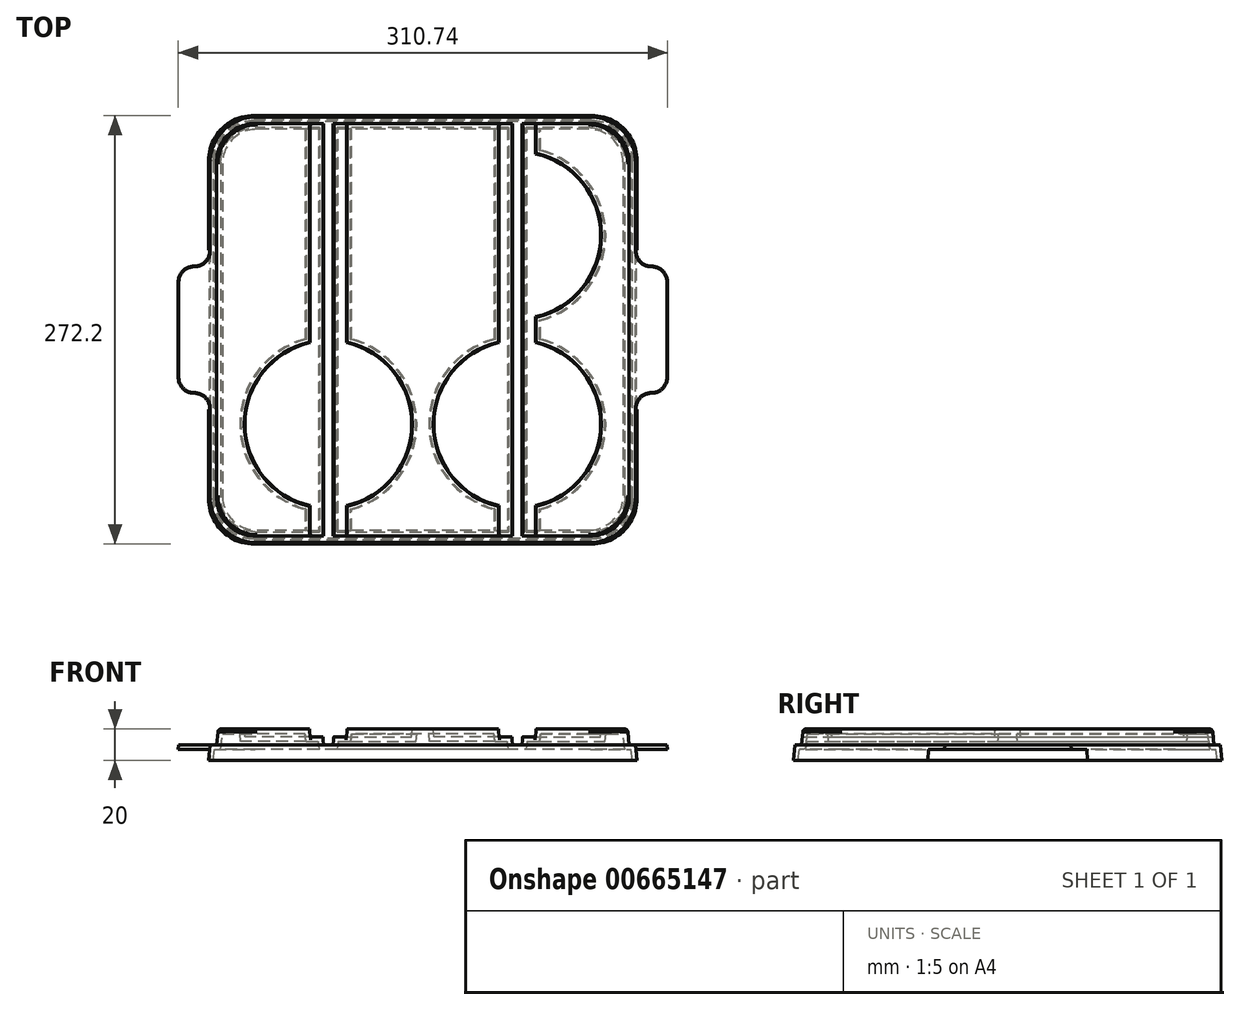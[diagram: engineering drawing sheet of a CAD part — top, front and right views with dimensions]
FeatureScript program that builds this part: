
annotation { "Feature Type Name" : "Feature", "Feature Type Description" : "" }
export const myFeature = defineFeature(function(context is Context, id is Id, definition is map)
    precondition{}
    {
        {
            var Q0;
            Q0=qCreatedBy(makeId("Top.planeOp"),FACE);
            var sketch = newSketch(context, id + "F0", { "sketchPlane" : qUnion([Q0])});
            skLineSegment(sketch, "E0", {"start": v(-60, 63.68) * mm, "end": v(-60, -68.5) * mm, "construction": true});
            skLineSegment(sketch, "E1", {"start": v(-108.87, 60) * mm, "end": v(91.95, 60) * mm, "construction": true});
            skLineSegment(sketch, "E2.MirrorCS", {"start": v(60, 63.68) * mm, "end": v(60, -68.5) * mm, "construction": true});
            skLineSegment(sketch, "E3.MirrorCS", {"start": v(-108.87, -60) * mm, "end": v(91.95, -60) * mm, "construction": true});
            skLineSegment(sketch, "E4", {"start": v(-130, 152.73) * mm, "end": v(-130, -156.18) * mm, "construction": true});
            skLineSegment(sketch, "E5", {"start": v(-201.2, -130) * mm, "end": v(310.8, -130) * mm, "construction": true});
            skLineSegment(sketch, "E6.MirrorCS", {"start": v(130, 152.73) * mm, "end": v(130, -156.18) * mm, "construction": true});
            skLineSegment(sketch, "E7.MirrorCS", {"start": v(-201.2, 130) * mm, "end": v(310.8, 130) * mm, "construction": true});
            skLineSegment(sketch, "E8.bottom", {"start": v(-130, 130) * mm, "end": v(130, 130) * mm});
            skLineSegment(sketch, "E8.top", {"start": v(-130, -130) * mm, "end": v(130, -130) * mm});
            skLineSegment(sketch, "E8.left", {"start": v(-130, 130) * mm, "end": v(-130, -130) * mm});
            skLineSegment(sketch, "E8.right", {"start": v(130, 130) * mm, "end": v(130, -130) * mm});
            skSolve(sketch);
        }
        {
            var Q0;
            Q0=makeQuery(id+"F0.imprint","IMPRINT",FACE,{"disambiguationData":[TD([[makeQuery(id+"F0.imprint","IMPRINT",EDGE,{"derivedFrom":sQuery(id+"F0.wireOp",EDGE,"E8.bottom")}),-1.0]])]});
            extrude(context, id + "F1", {"entities" : qUnion([Q0]), "oppositeDirection" : true, "depth" : 10 * mm, "offsetDistance" : 25 * mm, "hasDraft" : true, "draftAngle" : 6 * degree});
        }
        {
            var Q0;
            Q0=makeQuery(id+"F1.opExtrude","CAP_FACE",FACE,{"disambiguationData":[OSD([sQuery(id+"F0.wireOp",EDGE,"E8.bottom"),sQuery(id+"F0.wireOp",EDGE,"E8.top"),sQuery(id+"F0.wireOp",EDGE,"E8.left"),sQuery(id+"F0.wireOp",EDGE,"E8.right")])],"isStart":false});
            var sketch = newSketch(context, id + "F2", { "sketchPlane" : qUnion([Q0])});
            skLineSegment(sketch, "E9", {"start": v(-264, 135.05) * mm, "end": v(236, 135.05) * mm, "construction": true});
            skLineSegment(sketch, "E10.MirrorCS", {"start": v(-264, -135.05) * mm, "end": v(236, -135.05) * mm, "construction": true});
            skLineSegment(sketch, "E11", {"start": v(-135.05, 316.9) * mm, "end": v(-135.05, -183.1) * mm, "construction": true});
            skLineSegment(sketch, "E12.MirrorCS", {"start": v(135.05, 316.9) * mm, "end": v(135.05, -183.1) * mm, "construction": true});
            skLineSegment(sketch, "E13.bottom", {"start": v(-135.05, 135.05) * mm, "end": v(135.05, 135.05) * mm});
            skLineSegment(sketch, "E13.top", {"start": v(-135.05, -135.05) * mm, "end": v(135.05, -135.05) * mm});
            skLineSegment(sketch, "E13.left", {"start": v(-135.05, 135.05) * mm, "end": v(-135.05, -135.05) * mm});
            skLineSegment(sketch, "E13.right", {"start": v(135.05, 135.05) * mm, "end": v(135.05, -135.05) * mm});
            skSolve(sketch);
        }
        {
            var Q0;
            Q0=makeQuery(id+"F2.imprint","IMPRINT",FACE,{"disambiguationData":[TD([[makeQuery(id+"F2.imprint","IMPRINT",EDGE,{"derivedFrom":sQuery(id+"F2.wireOp",EDGE,"E13.bottom")}),-1.0]])]});
            var Q1;
            Q1=makeQuery(id+"F2.imprint","IMPRINT",FACE,{"disambiguationData":[TD([[makeQuery(id+"F2.imprint","IMPRINT",EDGE,{"derivedFrom":makeQuery(id+"F1.opExtrude","CAP_EDGE",EDGE,{"disambiguationData":[OSD([sQuery(id+"F0.wireOp",EDGE,"E8.bottom")])],"isStart":false})}),1.0]])]});
            extrude(context, id + "F3", {"entities" : qUnion([Q0, Q1]), "operationType" : NewBodyOperationType.ADD, "depth" : 10 * mm, "offsetDistance" : 25 * mm, "hasDraft" : true, "draftAngle" : 6 * degree});
        }
        {
            var Q0;
            Q0=makeQuery(id+"F1.opExtrude","CAP_FACE",FACE,{"disambiguationData":[OSD([sQuery(id+"F0.wireOp",EDGE,"E8.bottom"),sQuery(id+"F0.wireOp",EDGE,"E8.top"),sQuery(id+"F0.wireOp",EDGE,"E8.left"),sQuery(id+"F0.wireOp",EDGE,"E8.right")])],"isStart":true});
            var sketch = newSketch(context, id + "F4", { "sketchPlane" : qUnion([Q0])});
            skLineSegment(sketch, "E14", {"start": v(-130, 0) * mm, "end": v(130, 0) * mm, "construction": true});
            skLineSegment(sketch, "E15", {"start": v(-130, -60) * mm, "end": v(130, -60) * mm, "construction": true});
            skLineSegment(sketch, "E16.MirrorCS", {"start": v(-130, 60) * mm, "end": v(130, 60) * mm, "construction": true});
            skLineSegment(sketch, "E17", {"start": v(-60, -130) * mm, "end": v(-60, 130) * mm, "construction": true});
            skLineSegment(sketch, "E18", {"start": v(0, -130) * mm, "end": v(0, 130) * mm, "construction": true});
            skLineSegment(sketch, "E19.MirrorCS", {"start": v(60, -130) * mm, "end": v(60, 130) * mm, "construction": true});
            skCircle(sketch, "E20", {"center": v(-60, -60) * mm, "radius": 53.5 * mm});
            skCircle(sketch, "E21", {"center": v(-60, 60) * mm, "radius": 53.5 * mm});
            skCircle(sketch, "E22", {"center": v(60, 60) * mm, "radius": 53.5 * mm});
            skCircle(sketch, "E23", {"center": v(60, -60) * mm, "radius": 53.5 * mm});
            skLineSegment(sketch, "E24", {"start": v(72, 150) * mm, "end": v(72, 105.96) * mm});
            skLineSegment(sketch, "E25.MirrorCS", {"start": v(48, 130) * mm, "end": v(48, 105.96) * mm});
            skLineSegment(sketch, "E26.MirrorCS", {"start": v(-48, 130) * mm, "end": v(-48, 105.96) * mm});
            skLineSegment(sketch, "E27.MirrorCS", {"start": v(-72, 130) * mm, "end": v(-72, 105.96) * mm});
            skLineSegment(sketch, "E28.MirrorCS", {"start": v(48, -130) * mm, "end": v(48, -105.96) * mm});
            skLineSegment(sketch, "E29.MirrorCS", {"start": v(72, -130) * mm, "end": v(72, -105.96) * mm});
            skLineSegment(sketch, "E30.MirrorCS", {"start": v(-72, -130) * mm, "end": v(-72, -105.96) * mm});
            skLineSegment(sketch, "E31.MirrorCS", {"start": v(-48, -130) * mm, "end": v(-48, -105.96) * mm});
            skPoint(sketch, "E32.orphan", {"position": v(72, 130) * mm});
            skLineSegment(sketch, "E33.MirrorCS", {"start": v(48, 150) * mm, "end": v(48, 105.96) * mm});
            skLineSegment(sketch, "E34.MirrorCS", {"start": v(-48, 150) * mm, "end": v(-48, 105.96) * mm});
            skLineSegment(sketch, "E35.MirrorCS", {"start": v(-72, 150) * mm, "end": v(-72, 105.96) * mm});
            skLineSegment(sketch, "E36.MirrorCS", {"start": v(-48, -150) * mm, "end": v(-48, -105.96) * mm});
            skLineSegment(sketch, "E37.MirrorCS", {"start": v(-72, -150) * mm, "end": v(-72, -105.96) * mm});
            skLineSegment(sketch, "E38.MirrorCS", {"start": v(48, -150) * mm, "end": v(48, -105.96) * mm});
            skLineSegment(sketch, "E39.MirrorCS", {"start": v(72, -150) * mm, "end": v(72, -105.96) * mm});
            skLineSegment(sketch, "E40", {"start": v(-72, 150) * mm, "end": v(-48, 150) * mm});
            skLineSegment(sketch, "E41", {"start": v(48, 150) * mm, "end": v(72, 150) * mm});
            skLineSegment(sketch, "E42", {"start": v(-72, -150) * mm, "end": v(-48, -150) * mm});
            skLineSegment(sketch, "E43", {"start": v(48, -150) * mm, "end": v(72, -150) * mm});
            skLineSegment(sketch, "E44", {"start": v(-72, 105.96) * mm, "end": v(-72, -105.96) * mm});
            skLineSegment(sketch, "E45.MirrorCS", {"start": v(-48, 105.96) * mm, "end": v(-48, -105.96) * mm});
            skLineSegment(sketch, "E46.MirrorCS", {"start": v(48, 105.96) * mm, "end": v(48, -105.96) * mm});
            skLineSegment(sketch, "E47.MirrorCS", {"start": v(72, 105.96) * mm, "end": v(72, -105.96) * mm});
            skLineSegment(sketch, "E48", {"start": v(-64, 150) * mm, "end": v(-64, -150) * mm});
            skPoint(sketch, "E48.endSnap0", {"position": v(-60, -150) * mm});
            skLineSegment(sketch, "E49.MirrorCS", {"start": v(-56, 150) * mm, "end": v(-56, -150) * mm});
            skLineSegment(sketch, "E50.MirrorCS", {"start": v(56, 150) * mm, "end": v(56, -150) * mm});
            skLineSegment(sketch, "E51.MirrorCS", {"start": v(64, 150) * mm, "end": v(64, -150) * mm});
            skSolve(sketch);
        }
        {
            var Q0;
            {var subQ0=sQuery(id+"F4.wireOp",EDGE,"E34.MirrorCS");var subQ1=sQuery(id+"F4.wireOp",EDGE,"E21");var subQ2=makeQuery(id+"F4.imprint","INTERSECT",VERTEX,{"derivedFrom":[subQ1,subQ0]});Q0=makeQuery(id+"F4.imprint","IMPRINT",FACE,{"disambiguationData":[TD([[makeQuery(id+"F4.imprint","IMPRINT",EDGE,{"disambiguationData":[TD([[subQ2,1.0]])],"derivedFrom":subQ1}),1.0]])]});}
            var Q1;
            {var subQ0=sQuery(id+"F4.wireOp",EDGE,"E35.MirrorCS");var subQ1=sQuery(id+"F4.wireOp",EDGE,"E21");var subQ2=makeQuery(id+"F4.imprint","INTERSECT",VERTEX,{"derivedFrom":[subQ1,subQ0]});Q1=makeQuery(id+"F4.imprint","IMPRINT",FACE,{"disambiguationData":[TD([[makeQuery(id+"F4.imprint","IMPRINT",EDGE,{"disambiguationData":[TD([[subQ2,-1.0]])],"derivedFrom":subQ1}),1.0]])]});}
            var Q2;
            {var subQ3=sQuery(id+"F4.wireOp",EDGE,"E21");var subQ6=sQuery(id+"F4.wireOp",EDGE,"E48");var subQ7=makeQuery(id+"F4.imprint","INTERSECT",VERTEX,{"disambiguationData":[OD(0.0)],"derivedFrom":[subQ3,subQ6]});Q2=makeQuery(id+"F4.imprint","IMPRINT",FACE,{"disambiguationData":[TD([[makeQuery(id+"F4.imprint","IMPRINT",EDGE,{"disambiguationData":[TD([[subQ7,-1.0]])],"derivedFrom":subQ3}),1.0]])]});}
            var Q3;
            {var subQ3=sQuery(id+"F4.wireOp",EDGE,"E21");var subQ6=sQuery(id+"F4.wireOp",EDGE,"E49.MirrorCS");var subQ8=makeQuery(id+"F4.imprint","INTERSECT",VERTEX,{"disambiguationData":[OD(0.0)],"derivedFrom":[subQ3,subQ6]});Q3=makeQuery(id+"F4.imprint","IMPRINT",FACE,{"disambiguationData":[TD([[makeQuery(id+"F4.imprint","IMPRINT",EDGE,{"disambiguationData":[TD([[subQ8,1.0]])],"derivedFrom":subQ3}),1.0]])]});}
            var Q4;
            {var subQ0=sQuery(id+"F4.wireOp",EDGE,"E49.MirrorCS");var subQ1=sQuery(id+"F4.wireOp",EDGE,"E21");var subQ2=makeQuery(id+"F4.imprint","INTERSECT",VERTEX,{"disambiguationData":[OD(0.0)],"derivedFrom":[subQ1,subQ0]});Q4=makeQuery(id+"F4.imprint","IMPRINT",FACE,{"disambiguationData":[TD([[makeQuery(id+"F4.imprint","IMPRINT",EDGE,{"disambiguationData":[TD([[subQ2,-1.0]])],"derivedFrom":subQ1}),1.0]])]});}
            var Q5;
            {var subQ0=sQuery(id+"F4.wireOp",EDGE,"E33.MirrorCS");var subQ1=sQuery(id+"F4.wireOp",EDGE,"E22");var subQ2=makeQuery(id+"F4.imprint","INTERSECT",VERTEX,{"derivedFrom":[subQ1,subQ0]});Q5=makeQuery(id+"F4.imprint","IMPRINT",FACE,{"disambiguationData":[TD([[makeQuery(id+"F4.imprint","IMPRINT",EDGE,{"disambiguationData":[TD([[subQ2,-1.0]])],"derivedFrom":subQ1}),1.0]])]});}
            var Q6;
            {var subQ3=sQuery(id+"F4.wireOp",EDGE,"E22");var subQ5=sQuery(id+"F4.wireOp",EDGE,"E50.MirrorCS");var subQ6=makeQuery(id+"F4.imprint","INTERSECT",VERTEX,{"disambiguationData":[OD(0.0)],"derivedFrom":[subQ3,subQ5]});Q6=makeQuery(id+"F4.imprint","IMPRINT",FACE,{"disambiguationData":[TD([[makeQuery(id+"F4.imprint","IMPRINT",EDGE,{"disambiguationData":[TD([[subQ6,-1.0]])],"derivedFrom":subQ3}),1.0]])]});}
            var Q7;
            {var subQ3=sQuery(id+"F4.wireOp",EDGE,"E22");var subQ6=sQuery(id+"F4.wireOp",EDGE,"E51.MirrorCS");var subQ8=makeQuery(id+"F4.imprint","INTERSECT",VERTEX,{"disambiguationData":[OD(0.0)],"derivedFrom":[subQ3,subQ6]});Q7=makeQuery(id+"F4.imprint","IMPRINT",FACE,{"disambiguationData":[TD([[makeQuery(id+"F4.imprint","IMPRINT",EDGE,{"disambiguationData":[TD([[subQ8,1.0]])],"derivedFrom":subQ3}),1.0]])]});}
            var Q8;
            {var subQ0=sQuery(id+"F4.wireOp",EDGE,"E51.MirrorCS");var subQ1=sQuery(id+"F4.wireOp",EDGE,"E22");var subQ2=makeQuery(id+"F4.imprint","INTERSECT",VERTEX,{"disambiguationData":[OD(0.0)],"derivedFrom":[subQ1,subQ0]});Q8=makeQuery(id+"F4.imprint","IMPRINT",FACE,{"disambiguationData":[TD([[makeQuery(id+"F4.imprint","IMPRINT",EDGE,{"disambiguationData":[TD([[subQ2,-1.0]])],"derivedFrom":subQ1}),1.0]])]});}
            var Q9;
            {var subQ0=sQuery(id+"F4.wireOp",EDGE,"E24");var subQ1=sQuery(id+"F4.wireOp",EDGE,"E22");var subQ2=makeQuery(id+"F4.imprint","INTERSECT",VERTEX,{"derivedFrom":[subQ1,subQ0]});Q9=makeQuery(id+"F4.imprint","IMPRINT",FACE,{"disambiguationData":[TD([[makeQuery(id+"F4.imprint","IMPRINT",EDGE,{"disambiguationData":[TD([[subQ2,1.0]])],"derivedFrom":subQ1}),1.0]])]});}
            var Q10;
            {var subQ0=sQuery(id+"F4.wireOp",EDGE,"E44");var subQ1=sQuery(id+"F4.wireOp",EDGE,"E20");var subQ2=makeQuery(id+"F4.imprint","INTERSECT",VERTEX,{"derivedFrom":[subQ1,subQ0]});Q10=makeQuery(id+"F4.imprint","IMPRINT",FACE,{"disambiguationData":[TD([[makeQuery(id+"F4.imprint","IMPRINT",EDGE,{"disambiguationData":[TD([[subQ2,-1.0]])],"derivedFrom":subQ1}),1.0]])]});}
            var Q11;
            {var subQ3=sQuery(id+"F4.wireOp",EDGE,"E20");var subQ6=sQuery(id+"F4.wireOp",EDGE,"E48");var subQ8=makeQuery(id+"F4.imprint","INTERSECT",VERTEX,{"disambiguationData":[OD(0.0)],"derivedFrom":[subQ3,subQ6]});Q11=makeQuery(id+"F4.imprint","IMPRINT",FACE,{"disambiguationData":[TD([[makeQuery(id+"F4.imprint","IMPRINT",EDGE,{"disambiguationData":[TD([[subQ8,-1.0]])],"derivedFrom":subQ3}),1.0]])]});}
            var Q12;
            {var subQ0=sQuery(id+"F4.wireOp",EDGE,"E49.MirrorCS");var subQ1=sQuery(id+"F4.wireOp",EDGE,"E20");var subQ2=makeQuery(id+"F4.imprint","INTERSECT",VERTEX,{"disambiguationData":[OD(0.0)],"derivedFrom":[subQ1,subQ0]});Q12=makeQuery(id+"F4.imprint","IMPRINT",FACE,{"disambiguationData":[TD([[makeQuery(id+"F4.imprint","IMPRINT",EDGE,{"disambiguationData":[TD([[subQ2,-1.0]])],"derivedFrom":subQ1}),1.0]])]});}
            var Q13;
            {var subQ3=sQuery(id+"F4.wireOp",EDGE,"E20");var subQ6=sQuery(id+"F4.wireOp",EDGE,"E49.MirrorCS");var subQ8=makeQuery(id+"F4.imprint","INTERSECT",VERTEX,{"disambiguationData":[OD(0.0)],"derivedFrom":[subQ3,subQ6]});Q13=makeQuery(id+"F4.imprint","IMPRINT",FACE,{"disambiguationData":[TD([[makeQuery(id+"F4.imprint","IMPRINT",EDGE,{"disambiguationData":[TD([[subQ8,1.0]])],"derivedFrom":subQ3}),1.0]])]});}
            var Q14;
            {var subQ0=sQuery(id+"F4.wireOp",EDGE,"E45.MirrorCS");var subQ1=sQuery(id+"F4.wireOp",EDGE,"E20");var subQ2=makeQuery(id+"F4.imprint","INTERSECT",VERTEX,{"derivedFrom":[subQ1,subQ0]});Q14=makeQuery(id+"F4.imprint","IMPRINT",FACE,{"disambiguationData":[TD([[makeQuery(id+"F4.imprint","IMPRINT",EDGE,{"disambiguationData":[TD([[subQ2,1.0]])],"derivedFrom":subQ1}),1.0]])]});}
            var Q15;
            {var subQ0=sQuery(id+"F4.wireOp",EDGE,"E46.MirrorCS");var subQ1=sQuery(id+"F4.wireOp",EDGE,"E23");var subQ2=makeQuery(id+"F4.imprint","INTERSECT",VERTEX,{"derivedFrom":[subQ1,subQ0]});Q15=makeQuery(id+"F4.imprint","IMPRINT",FACE,{"disambiguationData":[TD([[makeQuery(id+"F4.imprint","IMPRINT",EDGE,{"disambiguationData":[TD([[subQ2,-1.0]])],"derivedFrom":subQ1}),1.0]])]});}
            var Q16;
            {var subQ3=sQuery(id+"F4.wireOp",EDGE,"E23");var subQ5=sQuery(id+"F4.wireOp",EDGE,"E50.MirrorCS");var subQ8=makeQuery(id+"F4.imprint","INTERSECT",VERTEX,{"disambiguationData":[OD(0.0)],"derivedFrom":[subQ3,subQ5]});Q16=makeQuery(id+"F4.imprint","IMPRINT",FACE,{"disambiguationData":[TD([[makeQuery(id+"F4.imprint","IMPRINT",EDGE,{"disambiguationData":[TD([[subQ8,-1.0]])],"derivedFrom":subQ3}),1.0]])]});}
            var Q17;
            {var subQ0=sQuery(id+"F4.wireOp",EDGE,"E51.MirrorCS");var subQ1=sQuery(id+"F4.wireOp",EDGE,"E23");var subQ2=makeQuery(id+"F4.imprint","INTERSECT",VERTEX,{"disambiguationData":[OD(0.0)],"derivedFrom":[subQ1,subQ0]});Q17=makeQuery(id+"F4.imprint","IMPRINT",FACE,{"disambiguationData":[TD([[makeQuery(id+"F4.imprint","IMPRINT",EDGE,{"disambiguationData":[TD([[subQ2,-1.0]])],"derivedFrom":subQ1}),1.0]])]});}
            var Q18;
            {var subQ3=sQuery(id+"F4.wireOp",EDGE,"E23");var subQ5=sQuery(id+"F4.wireOp",EDGE,"E51.MirrorCS");var subQ8=makeQuery(id+"F4.imprint","INTERSECT",VERTEX,{"disambiguationData":[OD(0.0)],"derivedFrom":[subQ3,subQ5]});Q18=makeQuery(id+"F4.imprint","IMPRINT",FACE,{"disambiguationData":[TD([[makeQuery(id+"F4.imprint","IMPRINT",EDGE,{"disambiguationData":[TD([[subQ8,1.0]])],"derivedFrom":subQ3}),1.0]])]});}
            var Q19;
            {var subQ0=sQuery(id+"F4.wireOp",EDGE,"E47.MirrorCS");var subQ1=sQuery(id+"F4.wireOp",EDGE,"E23");var subQ2=makeQuery(id+"F4.imprint","INTERSECT",VERTEX,{"derivedFrom":[subQ1,subQ0]});Q19=makeQuery(id+"F4.imprint","IMPRINT",FACE,{"disambiguationData":[TD([[makeQuery(id+"F4.imprint","IMPRINT",EDGE,{"disambiguationData":[TD([[subQ2,1.0]])],"derivedFrom":subQ1}),1.0]])]});}
            var Q20;
            {var subQ0=sQuery(id+"F4.wireOp",EDGE,"E48");var subQ1=sQuery(id+"F4.wireOp",EDGE,"E21");var subQ2=makeQuery(id+"F4.imprint","INTERSECT",VERTEX,{"disambiguationData":[OD(0.0)],"derivedFrom":[subQ1,subQ0]});Q20=makeQuery(id+"F4.imprint","IMPRINT",FACE,{"disambiguationData":[TD([[makeQuery(id+"F4.imprint","IMPRINT",EDGE,{"disambiguationData":[TD([[subQ2,-1.0]])],"derivedFrom":subQ1}),-1.0]])]});}
            var Q21;
            {var subQ0=sQuery(id+"F4.wireOp",EDGE,"E49.MirrorCS");var subQ1=sQuery(id+"F4.wireOp",EDGE,"E21");var subQ2=makeQuery(id+"F4.imprint","INTERSECT",VERTEX,{"disambiguationData":[OD(0.0)],"derivedFrom":[subQ1,subQ0]});Q21=makeQuery(id+"F4.imprint","IMPRINT",FACE,{"disambiguationData":[TD([[makeQuery(id+"F4.imprint","IMPRINT",EDGE,{"disambiguationData":[TD([[subQ2,-1.0]])],"derivedFrom":subQ1}),-1.0]])]});}
            var Q22;
            {var subQ0=sQuery(id+"F4.wireOp",EDGE,"E49.MirrorCS");var subQ1=sQuery(id+"F4.wireOp",EDGE,"E21");var subQ2=makeQuery(id+"F4.imprint","INTERSECT",VERTEX,{"disambiguationData":[OD(0.0)],"derivedFrom":[subQ1,subQ0]});Q22=makeQuery(id+"F4.imprint","IMPRINT",FACE,{"disambiguationData":[TD([[makeQuery(id+"F4.imprint","IMPRINT",EDGE,{"disambiguationData":[TD([[subQ2,1.0]])],"derivedFrom":subQ1}),-1.0]])]});}
            var Q23;
            {var subQ0=sQuery(id+"F4.wireOp",EDGE,"E40");var subQ1=sQuery(id+"F4.wireOp",EDGE,"E35.MirrorCS");var subQ2=makeQuery(id+"F4.imprint","INTERSECT",VERTEX,{"derivedFrom":[subQ1,subQ0]});Q23=makeQuery(id+"F4.imprint","IMPRINT",FACE,{"disambiguationData":[TD([[makeQuery(id+"F4.imprint","IMPRINT",EDGE,{"disambiguationData":[TD([[subQ2,-1.0]])],"derivedFrom":subQ1}),1.0]])]});}
            var Q24;
            {var subQ0=sQuery(id+"F4.wireOp",EDGE,"E48");var subQ1=sQuery(id+"F4.wireOp",EDGE,"E40");var subQ2=makeQuery(id+"F4.imprint","INTERSECT",VERTEX,{"derivedFrom":[subQ1,subQ0]});Q24=makeQuery(id+"F4.imprint","IMPRINT",FACE,{"disambiguationData":[TD([[makeQuery(id+"F4.imprint","IMPRINT",EDGE,{"disambiguationData":[TD([[subQ2,-1.0]])],"derivedFrom":subQ1}),-1.0]])]});}
            var Q25;
            {var subQ0=sQuery(id+"F4.wireOp",EDGE,"E40");var subQ1=sQuery(id+"F4.wireOp",EDGE,"E34.MirrorCS");var subQ2=makeQuery(id+"F4.imprint","INTERSECT",VERTEX,{"derivedFrom":[subQ1,subQ0]});Q25=makeQuery(id+"F4.imprint","IMPRINT",FACE,{"disambiguationData":[TD([[makeQuery(id+"F4.imprint","IMPRINT",EDGE,{"disambiguationData":[TD([[subQ2,-1.0]])],"derivedFrom":subQ1}),-1.0]])]});}
            var Q26;
            {var subQ0=sQuery(id+"F4.wireOp",EDGE,"E48");var subQ1=sQuery(id+"F4.wireOp",EDGE,"E20");var subQ2=makeQuery(id+"F4.imprint","INTERSECT",VERTEX,{"disambiguationData":[OD(0.0)],"derivedFrom":[subQ1,subQ0]});Q26=makeQuery(id+"F4.imprint","IMPRINT",FACE,{"disambiguationData":[TD([[makeQuery(id+"F4.imprint","IMPRINT",EDGE,{"disambiguationData":[TD([[subQ2,-1.0]])],"derivedFrom":subQ1}),-1.0]])]});}
            var Q27;
            {var subQ0=sQuery(id+"F4.wireOp",EDGE,"E49.MirrorCS");var subQ1=sQuery(id+"F4.wireOp",EDGE,"E20");var subQ2=makeQuery(id+"F4.imprint","INTERSECT",VERTEX,{"disambiguationData":[OD(0.0)],"derivedFrom":[subQ1,subQ0]});Q27=makeQuery(id+"F4.imprint","IMPRINT",FACE,{"disambiguationData":[TD([[makeQuery(id+"F4.imprint","IMPRINT",EDGE,{"disambiguationData":[TD([[subQ2,-1.0]])],"derivedFrom":subQ1}),-1.0]])]});}
            var Q28;
            {var subQ0=sQuery(id+"F4.wireOp",EDGE,"E49.MirrorCS");var subQ1=sQuery(id+"F4.wireOp",EDGE,"E20");var subQ2=makeQuery(id+"F4.imprint","INTERSECT",VERTEX,{"disambiguationData":[OD(0.0)],"derivedFrom":[subQ1,subQ0]});Q28=makeQuery(id+"F4.imprint","IMPRINT",FACE,{"disambiguationData":[TD([[makeQuery(id+"F4.imprint","IMPRINT",EDGE,{"disambiguationData":[TD([[subQ2,1.0]])],"derivedFrom":subQ1}),-1.0]])]});}
            var Q29;
            {var subQ0=sQuery(id+"F4.wireOp",EDGE,"E41");var subQ1=sQuery(id+"F4.wireOp",EDGE,"E33.MirrorCS");var subQ2=makeQuery(id+"F4.imprint","INTERSECT",VERTEX,{"derivedFrom":[subQ1,subQ0]});Q29=makeQuery(id+"F4.imprint","IMPRINT",FACE,{"disambiguationData":[TD([[makeQuery(id+"F4.imprint","IMPRINT",EDGE,{"disambiguationData":[TD([[subQ2,-1.0]])],"derivedFrom":subQ1}),1.0]])]});}
            var Q30;
            {var subQ0=sQuery(id+"F4.wireOp",EDGE,"E50.MirrorCS");var subQ1=sQuery(id+"F4.wireOp",EDGE,"E41");var subQ2=makeQuery(id+"F4.imprint","INTERSECT",VERTEX,{"derivedFrom":[subQ1,subQ0]});Q30=makeQuery(id+"F4.imprint","IMPRINT",FACE,{"disambiguationData":[TD([[makeQuery(id+"F4.imprint","IMPRINT",EDGE,{"disambiguationData":[TD([[subQ2,-1.0]])],"derivedFrom":subQ1}),-1.0]])]});}
            var Q31;
            {var subQ0=sQuery(id+"F4.wireOp",EDGE,"E41");var subQ1=sQuery(id+"F4.wireOp",EDGE,"E24");var subQ2=makeQuery(id+"F4.imprint","INTERSECT",VERTEX,{"derivedFrom":[subQ1,subQ0]});Q31=makeQuery(id+"F4.imprint","IMPRINT",FACE,{"disambiguationData":[TD([[makeQuery(id+"F4.imprint","IMPRINT",EDGE,{"disambiguationData":[TD([[subQ2,-1.0]])],"derivedFrom":subQ1}),-1.0]])]});}
            var Q32;
            {var subQ0=sQuery(id+"F4.wireOp",EDGE,"E50.MirrorCS");var subQ1=sQuery(id+"F4.wireOp",EDGE,"E22");var subQ2=makeQuery(id+"F4.imprint","INTERSECT",VERTEX,{"disambiguationData":[OD(0.0)],"derivedFrom":[subQ1,subQ0]});Q32=makeQuery(id+"F4.imprint","IMPRINT",FACE,{"disambiguationData":[TD([[makeQuery(id+"F4.imprint","IMPRINT",EDGE,{"disambiguationData":[TD([[subQ2,-1.0]])],"derivedFrom":subQ1}),-1.0]])]});}
            var Q33;
            {var subQ0=sQuery(id+"F4.wireOp",EDGE,"E51.MirrorCS");var subQ1=sQuery(id+"F4.wireOp",EDGE,"E22");var subQ2=makeQuery(id+"F4.imprint","INTERSECT",VERTEX,{"disambiguationData":[OD(0.0)],"derivedFrom":[subQ1,subQ0]});Q33=makeQuery(id+"F4.imprint","IMPRINT",FACE,{"disambiguationData":[TD([[makeQuery(id+"F4.imprint","IMPRINT",EDGE,{"disambiguationData":[TD([[subQ2,-1.0]])],"derivedFrom":subQ1}),-1.0]])]});}
            var Q34;
            {var subQ0=sQuery(id+"F4.wireOp",EDGE,"E51.MirrorCS");var subQ1=sQuery(id+"F4.wireOp",EDGE,"E22");var subQ2=makeQuery(id+"F4.imprint","INTERSECT",VERTEX,{"disambiguationData":[OD(0.0)],"derivedFrom":[subQ1,subQ0]});Q34=makeQuery(id+"F4.imprint","IMPRINT",FACE,{"disambiguationData":[TD([[makeQuery(id+"F4.imprint","IMPRINT",EDGE,{"disambiguationData":[TD([[subQ2,1.0]])],"derivedFrom":subQ1}),-1.0]])]});}
            var Q35;
            {var subQ0=sQuery(id+"F4.wireOp",EDGE,"E46.MirrorCS");var subQ1=sQuery(id+"F4.wireOp",EDGE,"E22");var subQ2=makeQuery(id+"F4.imprint","INTERSECT",VERTEX,{"derivedFrom":[subQ1,subQ0]});Q35=makeQuery(id+"F4.imprint","IMPRINT",FACE,{"disambiguationData":[TD([[makeQuery(id+"F4.imprint","IMPRINT",EDGE,{"disambiguationData":[TD([[subQ2,-1.0]])],"derivedFrom":subQ1}),-1.0]])]});}
            var Q36;
            {var subQ0=sQuery(id+"F4.wireOp",EDGE,"E50.MirrorCS");var subQ1=sQuery(id+"F4.wireOp",EDGE,"E22");var subQ2=makeQuery(id+"F4.imprint","INTERSECT",VERTEX,{"disambiguationData":[OD(1.0)],"derivedFrom":[subQ1,subQ0]});Q36=makeQuery(id+"F4.imprint","IMPRINT",FACE,{"disambiguationData":[TD([[makeQuery(id+"F4.imprint","IMPRINT",EDGE,{"disambiguationData":[TD([[subQ2,-1.0]])],"derivedFrom":subQ1}),-1.0]])]});}
            var Q37;
            {var subQ0=sQuery(id+"F4.wireOp",EDGE,"E51.MirrorCS");var subQ1=sQuery(id+"F4.wireOp",EDGE,"E22");var subQ2=makeQuery(id+"F4.imprint","INTERSECT",VERTEX,{"disambiguationData":[OD(1.0)],"derivedFrom":[subQ1,subQ0]});Q37=makeQuery(id+"F4.imprint","IMPRINT",FACE,{"disambiguationData":[TD([[makeQuery(id+"F4.imprint","IMPRINT",EDGE,{"disambiguationData":[TD([[subQ2,-1.0]])],"derivedFrom":subQ1}),-1.0]])]});}
            var Q38;
            {var subQ0=sQuery(id+"F4.wireOp",EDGE,"E42");var subQ1=sQuery(id+"F4.wireOp",EDGE,"E37.MirrorCS");var subQ2=makeQuery(id+"F4.imprint","INTERSECT",VERTEX,{"derivedFrom":[subQ1,subQ0]});Q38=makeQuery(id+"F4.imprint","IMPRINT",FACE,{"disambiguationData":[TD([[makeQuery(id+"F4.imprint","IMPRINT",EDGE,{"disambiguationData":[TD([[subQ2,-1.0]])],"derivedFrom":subQ1}),-1.0]])]});}
            var Q39;
            {var subQ0=sQuery(id+"F4.wireOp",EDGE,"E48");var subQ1=sQuery(id+"F4.wireOp",EDGE,"E42");var subQ2=makeQuery(id+"F4.imprint","INTERSECT",VERTEX,{"derivedFrom":[subQ1,subQ0]});Q39=makeQuery(id+"F4.imprint","IMPRINT",FACE,{"disambiguationData":[TD([[makeQuery(id+"F4.imprint","IMPRINT",EDGE,{"disambiguationData":[TD([[subQ2,-1.0]])],"derivedFrom":subQ1}),1.0]])]});}
            var Q40;
            {var subQ0=sQuery(id+"F4.wireOp",EDGE,"E42");var subQ1=sQuery(id+"F4.wireOp",EDGE,"E36.MirrorCS");var subQ2=makeQuery(id+"F4.imprint","INTERSECT",VERTEX,{"derivedFrom":[subQ1,subQ0]});Q40=makeQuery(id+"F4.imprint","IMPRINT",FACE,{"disambiguationData":[TD([[makeQuery(id+"F4.imprint","IMPRINT",EDGE,{"disambiguationData":[TD([[subQ2,-1.0]])],"derivedFrom":subQ1}),1.0]])]});}
            var Q41;
            {var subQ0=sQuery(id+"F4.wireOp",EDGE,"E37.MirrorCS");var subQ1=sQuery(id+"F4.wireOp",EDGE,"E20");var subQ2=makeQuery(id+"F4.imprint","INTERSECT",VERTEX,{"derivedFrom":[subQ1,subQ0]});Q41=makeQuery(id+"F4.imprint","IMPRINT",FACE,{"disambiguationData":[TD([[makeQuery(id+"F4.imprint","IMPRINT",EDGE,{"disambiguationData":[TD([[subQ2,-1.0]])],"derivedFrom":subQ1}),-1.0]])]});}
            var Q42;
            {var subQ0=sQuery(id+"F4.wireOp",EDGE,"E48");var subQ1=sQuery(id+"F4.wireOp",EDGE,"E20");var subQ2=makeQuery(id+"F4.imprint","INTERSECT",VERTEX,{"disambiguationData":[OD(1.0)],"derivedFrom":[subQ1,subQ0]});Q42=makeQuery(id+"F4.imprint","IMPRINT",FACE,{"disambiguationData":[TD([[makeQuery(id+"F4.imprint","IMPRINT",EDGE,{"disambiguationData":[TD([[subQ2,-1.0]])],"derivedFrom":subQ1}),-1.0]])]});}
            var Q43;
            {var subQ0=sQuery(id+"F4.wireOp",EDGE,"E49.MirrorCS");var subQ1=sQuery(id+"F4.wireOp",EDGE,"E20");var subQ2=makeQuery(id+"F4.imprint","INTERSECT",VERTEX,{"disambiguationData":[OD(1.0)],"derivedFrom":[subQ1,subQ0]});Q43=makeQuery(id+"F4.imprint","IMPRINT",FACE,{"disambiguationData":[TD([[makeQuery(id+"F4.imprint","IMPRINT",EDGE,{"disambiguationData":[TD([[subQ2,-1.0]])],"derivedFrom":subQ1}),-1.0]])]});}
            var Q44;
            {var subQ0=sQuery(id+"F4.wireOp",EDGE,"E38.MirrorCS");var subQ1=sQuery(id+"F4.wireOp",EDGE,"E23");var subQ2=makeQuery(id+"F4.imprint","INTERSECT",VERTEX,{"derivedFrom":[subQ1,subQ0]});Q44=makeQuery(id+"F4.imprint","IMPRINT",FACE,{"disambiguationData":[TD([[makeQuery(id+"F4.imprint","IMPRINT",EDGE,{"disambiguationData":[TD([[subQ2,-1.0]])],"derivedFrom":subQ1}),-1.0]])]});}
            var Q45;
            {var subQ0=sQuery(id+"F4.wireOp",EDGE,"E50.MirrorCS");var subQ1=sQuery(id+"F4.wireOp",EDGE,"E23");var subQ2=makeQuery(id+"F4.imprint","INTERSECT",VERTEX,{"disambiguationData":[OD(1.0)],"derivedFrom":[subQ1,subQ0]});Q45=makeQuery(id+"F4.imprint","IMPRINT",FACE,{"disambiguationData":[TD([[makeQuery(id+"F4.imprint","IMPRINT",EDGE,{"disambiguationData":[TD([[subQ2,-1.0]])],"derivedFrom":subQ1}),-1.0]])]});}
            var Q46;
            {var subQ0=sQuery(id+"F4.wireOp",EDGE,"E51.MirrorCS");var subQ1=sQuery(id+"F4.wireOp",EDGE,"E23");var subQ2=makeQuery(id+"F4.imprint","INTERSECT",VERTEX,{"disambiguationData":[OD(1.0)],"derivedFrom":[subQ1,subQ0]});Q46=makeQuery(id+"F4.imprint","IMPRINT",FACE,{"disambiguationData":[TD([[makeQuery(id+"F4.imprint","IMPRINT",EDGE,{"disambiguationData":[TD([[subQ2,-1.0]])],"derivedFrom":subQ1}),-1.0]])]});}
            var Q47;
            {var subQ0=sQuery(id+"F4.wireOp",EDGE,"E43");var subQ1=sQuery(id+"F4.wireOp",EDGE,"E38.MirrorCS");var subQ2=makeQuery(id+"F4.imprint","INTERSECT",VERTEX,{"derivedFrom":[subQ1,subQ0]});Q47=makeQuery(id+"F4.imprint","IMPRINT",FACE,{"disambiguationData":[TD([[makeQuery(id+"F4.imprint","IMPRINT",EDGE,{"disambiguationData":[TD([[subQ2,-1.0]])],"derivedFrom":subQ1}),-1.0]])]});}
            var Q48;
            {var subQ0=sQuery(id+"F4.wireOp",EDGE,"E50.MirrorCS");var subQ1=sQuery(id+"F4.wireOp",EDGE,"E43");var subQ2=makeQuery(id+"F4.imprint","INTERSECT",VERTEX,{"derivedFrom":[subQ1,subQ0]});Q48=makeQuery(id+"F4.imprint","IMPRINT",FACE,{"disambiguationData":[TD([[makeQuery(id+"F4.imprint","IMPRINT",EDGE,{"disambiguationData":[TD([[subQ2,-1.0]])],"derivedFrom":subQ1}),1.0]])]});}
            var Q49;
            {var subQ0=sQuery(id+"F4.wireOp",EDGE,"E43");var subQ1=sQuery(id+"F4.wireOp",EDGE,"E39.MirrorCS");var subQ2=makeQuery(id+"F4.imprint","INTERSECT",VERTEX,{"derivedFrom":[subQ1,subQ0]});Q49=makeQuery(id+"F4.imprint","IMPRINT",FACE,{"disambiguationData":[TD([[makeQuery(id+"F4.imprint","IMPRINT",EDGE,{"disambiguationData":[TD([[subQ2,-1.0]])],"derivedFrom":subQ1}),1.0]])]});}
            extrude(context, id + "F5", {"entities" : qUnion([Q0, Q1, Q2, Q3, Q4, Q5, Q6, Q7, Q8, Q9, Q10, Q11, Q12, Q13, Q14, Q15, Q16, Q17, Q18, Q19, Q20, Q21, Q22, Q23, Q24, Q25, Q26, Q27, Q28, Q29, Q30, Q31, Q32, Q33, Q34, Q35, Q36, Q37, Q38, Q39, Q40, Q41, Q42, Q43, Q44, Q45, Q46, Q47, Q48, Q49]), "operationType" : NewBodyOperationType.REMOVE, "oppositeDirection" : true, "depth" : 5 * mm, "offsetDistance" : 25 * mm, "hasDraft" : true, "draftAngle" : 6 * degree, "draftPullDirection" : true});
        }
        {
            var Q0;
            {var subQ0=sQuery(id+"F4.wireOp",EDGE,"E49.MirrorCS");var subQ1=sQuery(id+"F4.wireOp",EDGE,"E21");var subQ2=makeQuery(id+"F4.imprint","INTERSECT",VERTEX,{"disambiguationData":[OD(0.0)],"derivedFrom":[subQ1,subQ0]});Q0=makeQuery(id+"F4.imprint","IMPRINT",FACE,{"disambiguationData":[TD([[makeQuery(id+"F4.imprint","IMPRINT",EDGE,{"disambiguationData":[TD([[subQ2,-1.0]])],"derivedFrom":subQ1}),-1.0]])]});}
            var Q1;
            {var subQ0=sQuery(id+"F4.wireOp",EDGE,"E49.MirrorCS");var subQ1=sQuery(id+"F4.wireOp",EDGE,"E21");var subQ2=makeQuery(id+"F4.imprint","INTERSECT",VERTEX,{"disambiguationData":[OD(0.0)],"derivedFrom":[subQ1,subQ0]});Q1=makeQuery(id+"F4.imprint","IMPRINT",FACE,{"disambiguationData":[TD([[makeQuery(id+"F4.imprint","IMPRINT",EDGE,{"disambiguationData":[TD([[subQ2,-1.0]])],"derivedFrom":subQ1}),1.0]])]});}
            var Q2;
            {var subQ0=sQuery(id+"F4.wireOp",EDGE,"E49.MirrorCS");var subQ1=sQuery(id+"F4.wireOp",EDGE,"E20");var subQ2=makeQuery(id+"F4.imprint","INTERSECT",VERTEX,{"disambiguationData":[OD(0.0)],"derivedFrom":[subQ1,subQ0]});Q2=makeQuery(id+"F4.imprint","IMPRINT",FACE,{"disambiguationData":[TD([[makeQuery(id+"F4.imprint","IMPRINT",EDGE,{"disambiguationData":[TD([[subQ2,-1.0]])],"derivedFrom":subQ1}),-1.0]])]});}
            var Q3;
            {var subQ0=sQuery(id+"F4.wireOp",EDGE,"E49.MirrorCS");var subQ1=sQuery(id+"F4.wireOp",EDGE,"E20");var subQ2=makeQuery(id+"F4.imprint","INTERSECT",VERTEX,{"disambiguationData":[OD(0.0)],"derivedFrom":[subQ1,subQ0]});Q3=makeQuery(id+"F4.imprint","IMPRINT",FACE,{"disambiguationData":[TD([[makeQuery(id+"F4.imprint","IMPRINT",EDGE,{"disambiguationData":[TD([[subQ2,-1.0]])],"derivedFrom":subQ1}),1.0]])]});}
            var Q4;
            {var subQ0=sQuery(id+"F4.wireOp",EDGE,"E48");var subQ1=sQuery(id+"F4.wireOp",EDGE,"E20");var subQ2=makeQuery(id+"F4.imprint","INTERSECT",VERTEX,{"disambiguationData":[OD(1.0)],"derivedFrom":[subQ1,subQ0]});Q4=makeQuery(id+"F4.imprint","IMPRINT",FACE,{"disambiguationData":[TD([[makeQuery(id+"F4.imprint","IMPRINT",EDGE,{"disambiguationData":[TD([[subQ2,-1.0]])],"derivedFrom":subQ1}),-1.0]])]});}
            var Q5;
            {var subQ0=sQuery(id+"F4.wireOp",EDGE,"E51.MirrorCS");var subQ1=sQuery(id+"F4.wireOp",EDGE,"E23");var subQ2=makeQuery(id+"F4.imprint","INTERSECT",VERTEX,{"disambiguationData":[OD(0.0)],"derivedFrom":[subQ1,subQ0]});Q5=makeQuery(id+"F4.imprint","IMPRINT",FACE,{"disambiguationData":[TD([[makeQuery(id+"F4.imprint","IMPRINT",EDGE,{"disambiguationData":[TD([[subQ2,-1.0]])],"derivedFrom":subQ1}),1.0]])]});}
            var Q6;
            {var subQ0=sQuery(id+"F4.wireOp",EDGE,"E50.MirrorCS");var subQ1=sQuery(id+"F4.wireOp",EDGE,"E23");var subQ2=makeQuery(id+"F4.imprint","INTERSECT",VERTEX,{"disambiguationData":[OD(1.0)],"derivedFrom":[subQ1,subQ0]});Q6=makeQuery(id+"F4.imprint","IMPRINT",FACE,{"disambiguationData":[TD([[makeQuery(id+"F4.imprint","IMPRINT",EDGE,{"disambiguationData":[TD([[subQ2,-1.0]])],"derivedFrom":subQ1}),-1.0]])]});}
            var Q7;
            {var subQ0=sQuery(id+"F4.wireOp",EDGE,"E48");var subQ1=sQuery(id+"F4.wireOp",EDGE,"E42");var subQ2=makeQuery(id+"F4.imprint","INTERSECT",VERTEX,{"derivedFrom":[subQ1,subQ0]});Q7=makeQuery(id+"F4.imprint","IMPRINT",FACE,{"disambiguationData":[TD([[makeQuery(id+"F4.imprint","IMPRINT",EDGE,{"disambiguationData":[TD([[subQ2,-1.0]])],"derivedFrom":subQ1}),1.0]])]});}
            var Q8;
            {var subQ0=sQuery(id+"F4.wireOp",EDGE,"E50.MirrorCS");var subQ1=sQuery(id+"F4.wireOp",EDGE,"E43");var subQ2=makeQuery(id+"F4.imprint","INTERSECT",VERTEX,{"derivedFrom":[subQ1,subQ0]});Q8=makeQuery(id+"F4.imprint","IMPRINT",FACE,{"disambiguationData":[TD([[makeQuery(id+"F4.imprint","IMPRINT",EDGE,{"disambiguationData":[TD([[subQ2,-1.0]])],"derivedFrom":subQ1}),1.0]])]});}
            var Q9;
            {var subQ0=sQuery(id+"F4.wireOp",EDGE,"E50.MirrorCS");var subQ1=sQuery(id+"F4.wireOp",EDGE,"E22");var subQ2=makeQuery(id+"F4.imprint","INTERSECT",VERTEX,{"disambiguationData":[OD(1.0)],"derivedFrom":[subQ1,subQ0]});Q9=makeQuery(id+"F4.imprint","IMPRINT",FACE,{"disambiguationData":[TD([[makeQuery(id+"F4.imprint","IMPRINT",EDGE,{"disambiguationData":[TD([[subQ2,-1.0]])],"derivedFrom":subQ1}),-1.0]])]});}
            var Q10;
            {var subQ0=sQuery(id+"F4.wireOp",EDGE,"E51.MirrorCS");var subQ1=sQuery(id+"F4.wireOp",EDGE,"E22");var subQ2=makeQuery(id+"F4.imprint","INTERSECT",VERTEX,{"disambiguationData":[OD(0.0)],"derivedFrom":[subQ1,subQ0]});Q10=makeQuery(id+"F4.imprint","IMPRINT",FACE,{"disambiguationData":[TD([[makeQuery(id+"F4.imprint","IMPRINT",EDGE,{"disambiguationData":[TD([[subQ2,-1.0]])],"derivedFrom":subQ1}),1.0]])]});}
            var Q11;
            {var subQ0=sQuery(id+"F4.wireOp",EDGE,"E48");var subQ1=sQuery(id+"F4.wireOp",EDGE,"E40");var subQ2=makeQuery(id+"F4.imprint","INTERSECT",VERTEX,{"derivedFrom":[subQ1,subQ0]});Q11=makeQuery(id+"F4.imprint","IMPRINT",FACE,{"disambiguationData":[TD([[makeQuery(id+"F4.imprint","IMPRINT",EDGE,{"disambiguationData":[TD([[subQ2,-1.0]])],"derivedFrom":subQ1}),-1.0]])]});}
            var Q12;
            {var subQ0=sQuery(id+"F4.wireOp",EDGE,"E50.MirrorCS");var subQ1=sQuery(id+"F4.wireOp",EDGE,"E41");var subQ2=makeQuery(id+"F4.imprint","INTERSECT",VERTEX,{"derivedFrom":[subQ1,subQ0]});Q12=makeQuery(id+"F4.imprint","IMPRINT",FACE,{"disambiguationData":[TD([[makeQuery(id+"F4.imprint","IMPRINT",EDGE,{"disambiguationData":[TD([[subQ2,-1.0]])],"derivedFrom":subQ1}),-1.0]])]});}
            var Q13;
            {var subQ0=sQuery(id+"F4.wireOp",EDGE,"E51.MirrorCS");var subQ1=sQuery(id+"F4.wireOp",EDGE,"E22");var subQ2=makeQuery(id+"F4.imprint","INTERSECT",VERTEX,{"disambiguationData":[OD(0.0)],"derivedFrom":[subQ1,subQ0]});Q13=makeQuery(id+"F4.imprint","IMPRINT",FACE,{"disambiguationData":[TD([[makeQuery(id+"F4.imprint","IMPRINT",EDGE,{"disambiguationData":[TD([[subQ2,-1.0]])],"derivedFrom":subQ1}),-1.0]])]});}
            extrude(context, id + "F6", {"entities" : qUnion([Q0, Q1, Q2, Q3, Q4, Q5, Q6, Q7, Q8, Q9, Q10, Q11, Q12, Q13]), "operationType" : NewBodyOperationType.REMOVE, "oppositeDirection" : true, "depth" : 10 * mm, "offsetDistance" : 25 * mm, "hasDraft" : true, "draftAngle" : 6 * degree, "draftPullDirection" : true});
        }
        {
            var Q0;
            Q0=makeQuery(id+"F1.opExtrude","SWEPT_EDGE",EDGE,{"disambiguationData":[OSD([sQuery(id+"F0.wireOp",EDGE,"E8.top"),sQuery(id+"F0.wireOp",EDGE,"E8.left")])]});
            var Q1;
            Q1=makeQuery(id+"F1.opExtrude","SWEPT_EDGE",EDGE,{"disambiguationData":[OSD([sQuery(id+"F0.wireOp",EDGE,"E8.top"),sQuery(id+"F0.wireOp",EDGE,"E8.right")])]});
            var Q2;
            Q2=makeQuery(id+"F1.opExtrude","SWEPT_EDGE",EDGE,{"disambiguationData":[OSD([sQuery(id+"F0.wireOp",EDGE,"E8.bottom"),sQuery(id+"F0.wireOp",EDGE,"E8.right")])]});
            var Q3;
            Q3=makeQuery(id+"F1.opExtrude","SWEPT_EDGE",EDGE,{"disambiguationData":[OSD([sQuery(id+"F0.wireOp",EDGE,"E8.bottom"),sQuery(id+"F0.wireOp",EDGE,"E8.left")])]});
            fillet(context, id + "F7", {"entities" : qUnion([Q0, Q1, Q2, Q3]), "radius" : 25 * mm, "tangentPropagation" : true, "allowEdgeOverflow" : false});
        }
        {
            var Q0;
            Q0=makeQuery(id+"F3.opExtrude","SWEPT_EDGE",EDGE,{"disambiguationData":[OSD([sQuery(id+"F2.wireOp",EDGE,"E13.bottom"),sQuery(id+"F2.wireOp",EDGE,"E13.right")])]});
            var Q1;
            Q1=makeQuery(id+"F3.opExtrude","SWEPT_EDGE",EDGE,{"disambiguationData":[OSD([sQuery(id+"F2.wireOp",EDGE,"E13.top"),sQuery(id+"F2.wireOp",EDGE,"E13.right")])]});
            var Q2;
            Q2=makeQuery(id+"F3.opExtrude","SWEPT_EDGE",EDGE,{"disambiguationData":[OSD([sQuery(id+"F2.wireOp",EDGE,"E13.top"),sQuery(id+"F2.wireOp",EDGE,"E13.left")])]});
            var Q3;
            Q3=makeQuery(id+"F3.opExtrude","SWEPT_EDGE",EDGE,{"disambiguationData":[OSD([sQuery(id+"F2.wireOp",EDGE,"E13.bottom"),sQuery(id+"F2.wireOp",EDGE,"E13.left")])]});
            fillet(context, id + "F8", {"entities" : qUnion([Q0, Q1, Q2, Q3]), "radius" : 29 * mm, "tangentPropagation" : true, "allowEdgeOverflow" : false});
        }
        {
            var Q0;
            Q0=makeQuery(id+"F3.opExtrude","CAP_FACE",FACE,{"disambiguationData":[OSD([sQuery(id+"F2.wireOp",EDGE,"E13.bottom"),sQuery(id+"F2.wireOp",EDGE,"E13.top"),sQuery(id+"F2.wireOp",EDGE,"E13.left"),sQuery(id+"F2.wireOp",EDGE,"E13.right")])],"isStart":false});
            shell(context, id + "F9", {"entities" : qUnion([Q0]), "thickness" : 3 * mm});
        }
        {
            var Q0;
            Q0=makeQuery(id+"F1.opExtrude","CAP_EDGE",EDGE,{"disambiguationData":[OSD([sQuery(id+"F0.wireOp",EDGE,"E8.right")])],"isStart":true});
            var Q1;
            {var subQ0=sQuery(id+"F0.wireOp",EDGE,"E8.bottom");Q1=makeQuery(id+"FFMxlwrzM48GTUP_1.boolean.opBoolean","SPLIT",EDGE,{"disambiguationData":[TD([makeQuery(id+"FFMxlwrzM48GTUP_1.opExtrude","SWEPT_FACE",FACE,{"disambiguationData":[OSD([sQuery(id+"F4.wireOp",EDGE,"E33.MirrorCS")])]})])],"derivedFrom":makeQuery(id+"F1.opExtrude","CAP_EDGE",EDGE,{"disambiguationData":[OSD([subQ0])],"isStart":true})});}
            var Q2;
            Q2=makeQuery(id+"F1.opExtrude","CAP_EDGE",EDGE,{"disambiguationData":[OSD([sQuery(id+"F0.wireOp",EDGE,"E8.left")])],"isStart":true});
            var Q3;
            {var subQ0=sQuery(id+"F0.wireOp",EDGE,"E8.top");Q3=makeQuery(id+"FFMxlwrzM48GTUP_1.boolean.opBoolean","SPLIT",EDGE,{"disambiguationData":[TD([makeQuery(id+"FFMxlwrzM48GTUP_1.opExtrude","SWEPT_FACE",FACE,{"disambiguationData":[OSD([sQuery(id+"F4.wireOp",EDGE,"E36.MirrorCS")])]})])],"derivedFrom":makeQuery(id+"F1.opExtrude","CAP_EDGE",EDGE,{"disambiguationData":[OSD([subQ0])],"isStart":true})});}
            var Q4;
            {var subQ0=makeQuery(id+"F1.opExtrude","SWEPT_FACE",FACE,{"disambiguationData":[OSD([sQuery(id+"F0.wireOp",EDGE,"E8.top")])]});var subQ1=sQuery(id+"F4.wireOp",EDGE,"E37.MirrorCS");var subQ2=makeQuery(id+"F5.opExtrude","CAP_FACE",FACE,{"disambiguationData":[OSD([sQuery(id+"F4.wireOp",EDGE,"E20"),sQuery(id+"F4.wireOp",EDGE,"E21"),sQuery(id+"F4.wireOp",EDGE,"E34.MirrorCS"),sQuery(id+"F4.wireOp",EDGE,"E35.MirrorCS"),sQuery(id+"F4.wireOp",EDGE,"E36.MirrorCS"),subQ1,sQuery(id+"F4.wireOp",EDGE,"E40"),sQuery(id+"F4.wireOp",EDGE,"E42"),sQuery(id+"F4.wireOp",EDGE,"E44"),sQuery(id+"F4.wireOp",EDGE,"E45.MirrorCS")])],"isStart":false});Q4=makeQuery(id+"F6.boolean.opBoolean","SPLIT",EDGE,{"disambiguationData":[TD([makeQuery(id+"F5.boolean.opBoolean","COPY",FACE,{"derivedFrom":makeQuery(id+"F5.opExtrude","SWEPT_FACE",FACE,{"disambiguationData":[OSD([subQ1])]})})])],"derivedFrom":makeQuery(id+"F5.boolean.opBoolean","INTERSECT",EDGE,{"derivedFrom":[subQ0,subQ2]})});}
            var Q5;
            {var subQ0=makeQuery(id+"F1.opExtrude","SWEPT_FACE",FACE,{"disambiguationData":[OSD([sQuery(id+"F0.wireOp",EDGE,"E8.top")])]});var subQ1=sQuery(id+"F4.wireOp",EDGE,"E36.MirrorCS");var subQ2=makeQuery(id+"F5.opExtrude","CAP_FACE",FACE,{"disambiguationData":[OSD([sQuery(id+"F4.wireOp",EDGE,"E20"),sQuery(id+"F4.wireOp",EDGE,"E21"),sQuery(id+"F4.wireOp",EDGE,"E34.MirrorCS"),sQuery(id+"F4.wireOp",EDGE,"E35.MirrorCS"),subQ1,sQuery(id+"F4.wireOp",EDGE,"E37.MirrorCS"),sQuery(id+"F4.wireOp",EDGE,"E40"),sQuery(id+"F4.wireOp",EDGE,"E42"),sQuery(id+"F4.wireOp",EDGE,"E44"),sQuery(id+"F4.wireOp",EDGE,"E45.MirrorCS")])],"isStart":false});Q5=makeQuery(id+"F6.boolean.opBoolean","SPLIT",EDGE,{"disambiguationData":[TD([makeQuery(id+"F5.boolean.opBoolean","COPY",FACE,{"derivedFrom":makeQuery(id+"F5.opExtrude","SWEPT_FACE",FACE,{"disambiguationData":[OSD([subQ1])]})})])],"derivedFrom":makeQuery(id+"F5.boolean.opBoolean","INTERSECT",EDGE,{"derivedFrom":[subQ0,subQ2]})});}
            var Q6;
            {var subQ0=makeQuery(id+"F1.opExtrude","SWEPT_FACE",FACE,{"disambiguationData":[OSD([sQuery(id+"F0.wireOp",EDGE,"E8.top")])]});var subQ1=sQuery(id+"F4.wireOp",EDGE,"E38.MirrorCS");var subQ2=makeQuery(id+"F5.opExtrude","CAP_FACE",FACE,{"disambiguationData":[OSD([sQuery(id+"F4.wireOp",EDGE,"E22"),sQuery(id+"F4.wireOp",EDGE,"E23"),sQuery(id+"F4.wireOp",EDGE,"E24"),sQuery(id+"F4.wireOp",EDGE,"E33.MirrorCS"),subQ1,sQuery(id+"F4.wireOp",EDGE,"E39.MirrorCS"),sQuery(id+"F4.wireOp",EDGE,"E41"),sQuery(id+"F4.wireOp",EDGE,"E43"),sQuery(id+"F4.wireOp",EDGE,"E46.MirrorCS"),sQuery(id+"F4.wireOp",EDGE,"E47.MirrorCS")])],"isStart":false});Q6=makeQuery(id+"F6.boolean.opBoolean","SPLIT",EDGE,{"disambiguationData":[TD([makeQuery(id+"F5.boolean.opBoolean","COPY",FACE,{"derivedFrom":makeQuery(id+"F5.opExtrude","SWEPT_FACE",FACE,{"disambiguationData":[OSD([subQ1])]})})])],"derivedFrom":makeQuery(id+"F5.boolean.opBoolean","INTERSECT",EDGE,{"derivedFrom":[subQ0,subQ2]})});}
            var Q7;
            {var subQ0=makeQuery(id+"F1.opExtrude","SWEPT_FACE",FACE,{"disambiguationData":[OSD([sQuery(id+"F0.wireOp",EDGE,"E8.top")])]});var subQ1=sQuery(id+"F4.wireOp",EDGE,"E39.MirrorCS");var subQ2=makeQuery(id+"F5.opExtrude","CAP_FACE",FACE,{"disambiguationData":[OSD([sQuery(id+"F4.wireOp",EDGE,"E22"),sQuery(id+"F4.wireOp",EDGE,"E23"),sQuery(id+"F4.wireOp",EDGE,"E24"),sQuery(id+"F4.wireOp",EDGE,"E33.MirrorCS"),sQuery(id+"F4.wireOp",EDGE,"E38.MirrorCS"),subQ1,sQuery(id+"F4.wireOp",EDGE,"E41"),sQuery(id+"F4.wireOp",EDGE,"E43"),sQuery(id+"F4.wireOp",EDGE,"E46.MirrorCS"),sQuery(id+"F4.wireOp",EDGE,"E47.MirrorCS")])],"isStart":false});Q7=makeQuery(id+"F6.boolean.opBoolean","SPLIT",EDGE,{"disambiguationData":[TD([makeQuery(id+"F5.boolean.opBoolean","COPY",FACE,{"derivedFrom":makeQuery(id+"F5.opExtrude","SWEPT_FACE",FACE,{"disambiguationData":[OSD([subQ1])]})})])],"derivedFrom":makeQuery(id+"F5.boolean.opBoolean","INTERSECT",EDGE,{"derivedFrom":[subQ0,subQ2]})});}
            var Q8;
            {var subQ0=makeQuery(id+"F1.opExtrude","SWEPT_FACE",FACE,{"disambiguationData":[OSD([sQuery(id+"F0.wireOp",EDGE,"E8.bottom")])]});var subQ1=sQuery(id+"F4.wireOp",EDGE,"E35.MirrorCS");var subQ2=makeQuery(id+"F5.opExtrude","CAP_FACE",FACE,{"disambiguationData":[OSD([sQuery(id+"F4.wireOp",EDGE,"E20"),sQuery(id+"F4.wireOp",EDGE,"E21"),sQuery(id+"F4.wireOp",EDGE,"E34.MirrorCS"),subQ1,sQuery(id+"F4.wireOp",EDGE,"E36.MirrorCS"),sQuery(id+"F4.wireOp",EDGE,"E37.MirrorCS"),sQuery(id+"F4.wireOp",EDGE,"E40"),sQuery(id+"F4.wireOp",EDGE,"E42"),sQuery(id+"F4.wireOp",EDGE,"E44"),sQuery(id+"F4.wireOp",EDGE,"E45.MirrorCS")])],"isStart":false});Q8=makeQuery(id+"F6.boolean.opBoolean","SPLIT",EDGE,{"disambiguationData":[TD([makeQuery(id+"F5.boolean.opBoolean","COPY",FACE,{"derivedFrom":makeQuery(id+"F5.opExtrude","SWEPT_FACE",FACE,{"disambiguationData":[OSD([subQ1])]})})])],"derivedFrom":makeQuery(id+"F5.boolean.opBoolean","INTERSECT",EDGE,{"derivedFrom":[subQ0,subQ2]})});}
            var Q9;
            {var subQ0=makeQuery(id+"F1.opExtrude","SWEPT_FACE",FACE,{"disambiguationData":[OSD([sQuery(id+"F0.wireOp",EDGE,"E8.bottom")])]});var subQ1=sQuery(id+"F4.wireOp",EDGE,"E34.MirrorCS");var subQ2=makeQuery(id+"F5.opExtrude","CAP_FACE",FACE,{"disambiguationData":[OSD([sQuery(id+"F4.wireOp",EDGE,"E20"),sQuery(id+"F4.wireOp",EDGE,"E21"),subQ1,sQuery(id+"F4.wireOp",EDGE,"E35.MirrorCS"),sQuery(id+"F4.wireOp",EDGE,"E36.MirrorCS"),sQuery(id+"F4.wireOp",EDGE,"E37.MirrorCS"),sQuery(id+"F4.wireOp",EDGE,"E40"),sQuery(id+"F4.wireOp",EDGE,"E42"),sQuery(id+"F4.wireOp",EDGE,"E44"),sQuery(id+"F4.wireOp",EDGE,"E45.MirrorCS")])],"isStart":false});Q9=makeQuery(id+"F6.boolean.opBoolean","SPLIT",EDGE,{"disambiguationData":[TD([makeQuery(id+"F5.boolean.opBoolean","COPY",FACE,{"derivedFrom":makeQuery(id+"F5.opExtrude","SWEPT_FACE",FACE,{"disambiguationData":[OSD([subQ1])]})})])],"derivedFrom":makeQuery(id+"F5.boolean.opBoolean","INTERSECT",EDGE,{"derivedFrom":[subQ0,subQ2]})});}
            var Q10;
            {var subQ0=makeQuery(id+"F1.opExtrude","SWEPT_FACE",FACE,{"disambiguationData":[OSD([sQuery(id+"F0.wireOp",EDGE,"E8.bottom")])]});var subQ1=sQuery(id+"F4.wireOp",EDGE,"E33.MirrorCS");var subQ2=makeQuery(id+"F5.opExtrude","CAP_FACE",FACE,{"disambiguationData":[OSD([sQuery(id+"F4.wireOp",EDGE,"E22"),sQuery(id+"F4.wireOp",EDGE,"E23"),sQuery(id+"F4.wireOp",EDGE,"E24"),subQ1,sQuery(id+"F4.wireOp",EDGE,"E38.MirrorCS"),sQuery(id+"F4.wireOp",EDGE,"E39.MirrorCS"),sQuery(id+"F4.wireOp",EDGE,"E41"),sQuery(id+"F4.wireOp",EDGE,"E43"),sQuery(id+"F4.wireOp",EDGE,"E46.MirrorCS"),sQuery(id+"F4.wireOp",EDGE,"E47.MirrorCS")])],"isStart":false});Q10=makeQuery(id+"F6.boolean.opBoolean","SPLIT",EDGE,{"disambiguationData":[TD([makeQuery(id+"F5.boolean.opBoolean","COPY",FACE,{"derivedFrom":makeQuery(id+"F5.opExtrude","SWEPT_FACE",FACE,{"disambiguationData":[OSD([subQ1])]})})])],"derivedFrom":makeQuery(id+"F5.boolean.opBoolean","INTERSECT",EDGE,{"derivedFrom":[subQ0,subQ2]})});}
            var Q11;
            {var subQ0=makeQuery(id+"F1.opExtrude","SWEPT_FACE",FACE,{"disambiguationData":[OSD([sQuery(id+"F0.wireOp",EDGE,"E8.bottom")])]});var subQ1=sQuery(id+"F4.wireOp",EDGE,"E24");var subQ2=makeQuery(id+"F5.opExtrude","CAP_FACE",FACE,{"disambiguationData":[OSD([sQuery(id+"F4.wireOp",EDGE,"E22"),sQuery(id+"F4.wireOp",EDGE,"E23"),subQ1,sQuery(id+"F4.wireOp",EDGE,"E33.MirrorCS"),sQuery(id+"F4.wireOp",EDGE,"E38.MirrorCS"),sQuery(id+"F4.wireOp",EDGE,"E39.MirrorCS"),sQuery(id+"F4.wireOp",EDGE,"E41"),sQuery(id+"F4.wireOp",EDGE,"E43"),sQuery(id+"F4.wireOp",EDGE,"E46.MirrorCS"),sQuery(id+"F4.wireOp",EDGE,"E47.MirrorCS")])],"isStart":false});Q11=makeQuery(id+"F6.boolean.opBoolean","SPLIT",EDGE,{"disambiguationData":[TD([makeQuery(id+"F5.boolean.opBoolean","COPY",FACE,{"derivedFrom":makeQuery(id+"F5.opExtrude","SWEPT_FACE",FACE,{"disambiguationData":[OSD([subQ1])]})})])],"derivedFrom":makeQuery(id+"F5.boolean.opBoolean","INTERSECT",EDGE,{"derivedFrom":[subQ0,subQ2]})});}
            fillet(context, id + "F10", {"entities" : qUnion([Q0, Q1, Q2, Q3, Q4, Q5, Q6, Q7, Q8, Q9, Q10, Q11]), "radius" : 2 * mm, "tangentPropagation" : true, "allowEdgeOverflow" : false});
        }
        {
            var Q0;
            Q0=makeQuery(id+"FFMxlwrzM48GTUP_1.boolean.opBoolean","MERGE",FACE,{"derivedFrom":[makeQuery(id+"F3.opExtrude","CAP_FACE",FACE,{"disambiguationData":[OSD([sQuery(id+"F2.wireOp",EDGE,"E13.bottom"),sQuery(id+"F2.wireOp",EDGE,"E13.top"),sQuery(id+"F2.wireOp",EDGE,"E13.left"),sQuery(id+"F2.wireOp",EDGE,"E13.right")])],"isStart":true}),makeQuery(id+"FFMxlwrzM48GTUP_1.opExtrude","CAP_FACE",FACE,{"disambiguationData":[OSD([sQuery(id+"F4.wireOp",EDGE,"E24"),sQuery(id+"F4.wireOp",EDGE,"0tpGAXtC-clnW-DzUJ-E4Gk-3UYplvxCWuQU"),sQuery(id+"F4.wireOp",EDGE,"E33.MirrorCS"),sQuery(id+"F4.wireOp",EDGE,"E41")])],"isStart":false}),makeQuery(id+"FFMxlwrzM48GTUP_1.opExtrude","CAP_FACE",FACE,{"disambiguationData":[OSD([sQuery(id+"F4.wireOp",EDGE,"6fd3e808-e90c-4549-8836-5e467082efef0.MirrorCS"),sQuery(id+"F4.wireOp",EDGE,"E34.MirrorCS"),sQuery(id+"F4.wireOp",EDGE,"E35.MirrorCS"),sQuery(id+"F4.wireOp",EDGE,"E40")])],"isStart":false}),makeQuery(id+"FFMxlwrzM48GTUP_1.opExtrude","CAP_FACE",FACE,{"disambiguationData":[OSD([sQuery(id+"F4.wireOp",EDGE,"e49ff9fc-5064-4601-90bc-e5e2885164bb0.MirrorCS"),sQuery(id+"F4.wireOp",EDGE,"E36.MirrorCS"),sQuery(id+"F4.wireOp",EDGE,"E37.MirrorCS"),sQuery(id+"F4.wireOp",EDGE,"E42")])],"isStart":false}),makeQuery(id+"FFMxlwrzM48GTUP_1.opExtrude","CAP_FACE",FACE,{"disambiguationData":[OSD([sQuery(id+"F4.wireOp",EDGE,"446428ba-9815-4af7-82a4-81c271596e950.MirrorCS"),sQuery(id+"F4.wireOp",EDGE,"E38.MirrorCS"),sQuery(id+"F4.wireOp",EDGE,"E39.MirrorCS"),sQuery(id+"F4.wireOp",EDGE,"E43")])],"isStart":false})]});
            var sketch = newSketch(context, id + "F11", { "sketchPlane" : qUnion([Q0])});
            skLineSegment(sketch, "E52", {"start": v(-135.05, 0) * mm, "end": v(-209.56, 0) * mm, "construction": true});
            skLineSegment(sketch, "E53", {"start": v(-135.05, 40) * mm, "end": v(-155.05, 40) * mm});
            skLineSegment(sketch, "E54.MirrorCS", {"start": v(-135.05, -40) * mm, "end": v(-155.05, -40) * mm});
            skLineSegment(sketch, "E55", {"start": v(-155.05, 40) * mm, "end": v(-155.05, -40) * mm});
            skLineSegment(sketch, "E56.MirrorCS", {"start": v(155.05, 40) * mm, "end": v(155.05, -40) * mm});
            skLineSegment(sketch, "E57.MirrorCS", {"start": v(135.05, 40) * mm, "end": v(155.05, 40) * mm});
            skLineSegment(sketch, "E58.MirrorCS", {"start": v(135.05, -40) * mm, "end": v(155.05, -40) * mm});
            skSolve(sketch);
        }
        {
            var Q0;
            {var subQ0=sQuery(id+"F11.wireOp",EDGE,"E53");Q0=makeQuery(id+"F11.imprint","IMPRINT",FACE,{"disambiguationData":[TD([[makeQuery(id+"F11.imprint","IMPRINT",EDGE,{"derivedFrom":subQ0}),1.0]])]});}
            var Q1;
            Q1=makeQuery(id+"F11.imprint","IMPRINT",FACE,{"disambiguationData":[TD([[makeQuery(id+"F11.imprint","IMPRINT",EDGE,{"derivedFrom":sQuery(id+"F11.wireOp",EDGE,"E56.MirrorCS")}),-1.0]])]});
            extrude(context, id + "F12", {"entities" : qUnion([Q0, Q1]), "operationType" : NewBodyOperationType.ADD, "oppositeDirection" : true, "depth" : 3 * mm, "offsetDistance" : 25 * mm, "hasDraft" : true, "draftAngle" : 6 * degree});
        }
        {
            var Q0;
            Q0=makeQuery(id+"F12.boolean.opBoolean","INTERSECT",EDGE,{"derivedFrom":[makeQuery(id+"F3.opExtrude","SWEPT_FACE",FACE,{"disambiguationData":[OSD([sQuery(id+"F2.wireOp",EDGE,"E13.left")])]}),makeQuery(id+"F12.opExtrude","SWEPT_FACE",FACE,{"disambiguationData":[OSD([sQuery(id+"F11.wireOp",EDGE,"E54.MirrorCS")])]})]});
            var Q1;
            Q1=makeQuery(id+"F12.boolean.opBoolean","INTERSECT",EDGE,{"derivedFrom":[makeQuery(id+"F3.opExtrude","SWEPT_FACE",FACE,{"disambiguationData":[OSD([sQuery(id+"F2.wireOp",EDGE,"E13.left")])]}),makeQuery(id+"F12.opExtrude","SWEPT_FACE",FACE,{"disambiguationData":[OSD([sQuery(id+"F11.wireOp",EDGE,"E53")])]})]});
            var Q2;
            Q2=makeQuery(id+"F12.opExtrude","SWEPT_EDGE",EDGE,{"disambiguationData":[OSD([sQuery(id+"F11.wireOp",EDGE,"E53"),sQuery(id+"F11.wireOp",EDGE,"E55")])]});
            var Q3;
            Q3=makeQuery(id+"F12.opExtrude","SWEPT_EDGE",EDGE,{"disambiguationData":[OSD([sQuery(id+"F11.wireOp",EDGE,"E54.MirrorCS"),sQuery(id+"F11.wireOp",EDGE,"E55")])]});
            var Q4;
            Q4=makeQuery(id+"F12.opExtrude","SWEPT_EDGE",EDGE,{"disambiguationData":[OSD([sQuery(id+"F11.wireOp",EDGE,"E56.MirrorCS"),sQuery(id+"F11.wireOp",EDGE,"E58.MirrorCS")])]});
            var Q5;
            Q5=makeQuery(id+"F12.boolean.opBoolean","INTERSECT",EDGE,{"derivedFrom":[makeQuery(id+"F3.opExtrude","SWEPT_FACE",FACE,{"disambiguationData":[OSD([sQuery(id+"F2.wireOp",EDGE,"E13.right")])]}),makeQuery(id+"F12.opExtrude","SWEPT_FACE",FACE,{"disambiguationData":[OSD([sQuery(id+"F11.wireOp",EDGE,"E58.MirrorCS")])]})]});
            var Q6;
            Q6=makeQuery(id+"F12.boolean.opBoolean","INTERSECT",EDGE,{"derivedFrom":[makeQuery(id+"F3.opExtrude","SWEPT_FACE",FACE,{"disambiguationData":[OSD([sQuery(id+"F2.wireOp",EDGE,"E13.right")])]}),makeQuery(id+"F12.opExtrude","SWEPT_FACE",FACE,{"disambiguationData":[OSD([sQuery(id+"F11.wireOp",EDGE,"E57.MirrorCS")])]})]});
            var Q7;
            Q7=makeQuery(id+"F12.opExtrude","SWEPT_EDGE",EDGE,{"disambiguationData":[OSD([sQuery(id+"F11.wireOp",EDGE,"E56.MirrorCS"),sQuery(id+"F11.wireOp",EDGE,"E57.MirrorCS")])]});
            fillet(context, id + "F13", {"entities" : qUnion([Q0, Q1, Q2, Q3, Q4, Q5, Q6, Q7]), "radius" : 10 * mm, "tangentPropagation" : true, "allowEdgeOverflow" : false});
        }
        {
            var Q0;
            Q0=makeQuery(id+"F12.opExtrude","CAP_FACE",FACE,{"disambiguationData":[OSD([sQuery(id+"F2.wireOp",EDGE,"E13.left"),sQuery(id+"F11.wireOp",EDGE,"E53"),sQuery(id+"F11.wireOp",EDGE,"E54.MirrorCS"),sQuery(id+"F11.wireOp",EDGE,"E55")])],"isStart":false});
            var sketch = newSketch(context, id + "F14", { "sketchPlane" : qUnion([Q0])});
            skPoint(sketch, "E59", {"position": v(-135.37, 50.26) * mm});
            skPoint(sketch, "E60", {"position": v(-135.37, -50.26) * mm});
            skLineSegment(sketch, "E61", {"start": v(-135.37, -50.26) * mm, "end": v(-177, -50.26) * mm, "construction": true});
            skLineSegment(sketch, "E62", {"start": v(0, 90.37) * mm, "end": v(0, -86.26) * mm, "construction": true});
            skPoint(sketch, "E63.MirrorP", {"position": v(135.37, 50.26) * mm});
            skPoint(sketch, "E64.MirrorP", {"position": v(135.37, -50.26) * mm});
            skLineSegment(sketch, "E65.MirrorCS", {"start": v(135.37, -50.26) * mm, "end": v(177, -50.26) * mm, "construction": true});
            skLineSegment(sketch, "E66.bottom", {"start": v(-135.37, 50.26) * mm, "end": v(-165.37, 50.26) * mm});
            skLineSegment(sketch, "E66.top", {"start": v(-135.37, -50.26) * mm, "end": v(-165.37, -50.26) * mm});
            skLineSegment(sketch, "E66.left", {"start": v(-135.37, 50.26) * mm, "end": v(-135.37, -50.26) * mm});
            skLineSegment(sketch, "E66.right", {"start": v(-165.37, 50.26) * mm, "end": v(-165.37, -50.26) * mm});
            skLineSegment(sketch, "E67.bottom", {"start": v(135.37, 50.26) * mm, "end": v(165.37, 50.26) * mm});
            skLineSegment(sketch, "E67.top", {"start": v(135.37, -50.26) * mm, "end": v(165.37, -50.26) * mm});
            skLineSegment(sketch, "E67.left", {"start": v(135.37, 50.26) * mm, "end": v(135.37, -50.26) * mm});
            skLineSegment(sketch, "E67.right", {"start": v(165.37, 50.26) * mm, "end": v(165.37, -50.26) * mm});
            skSolve(sketch);
        }
        {
            var Q0;
            Q0 = qSketchRegion(id + "F14", true);
            extrude(context, id + "F15", {"entities" : qUnion([Q0]), "operationType" : NewBodyOperationType.REMOVE, "endBound" : BoundingType.THROUGH_ALL, "depth" : 25 * mm, "offsetDistance" : 25 * mm, "hasDraft" : true, "draftAngle" : 3 * degree});
        }
    });
